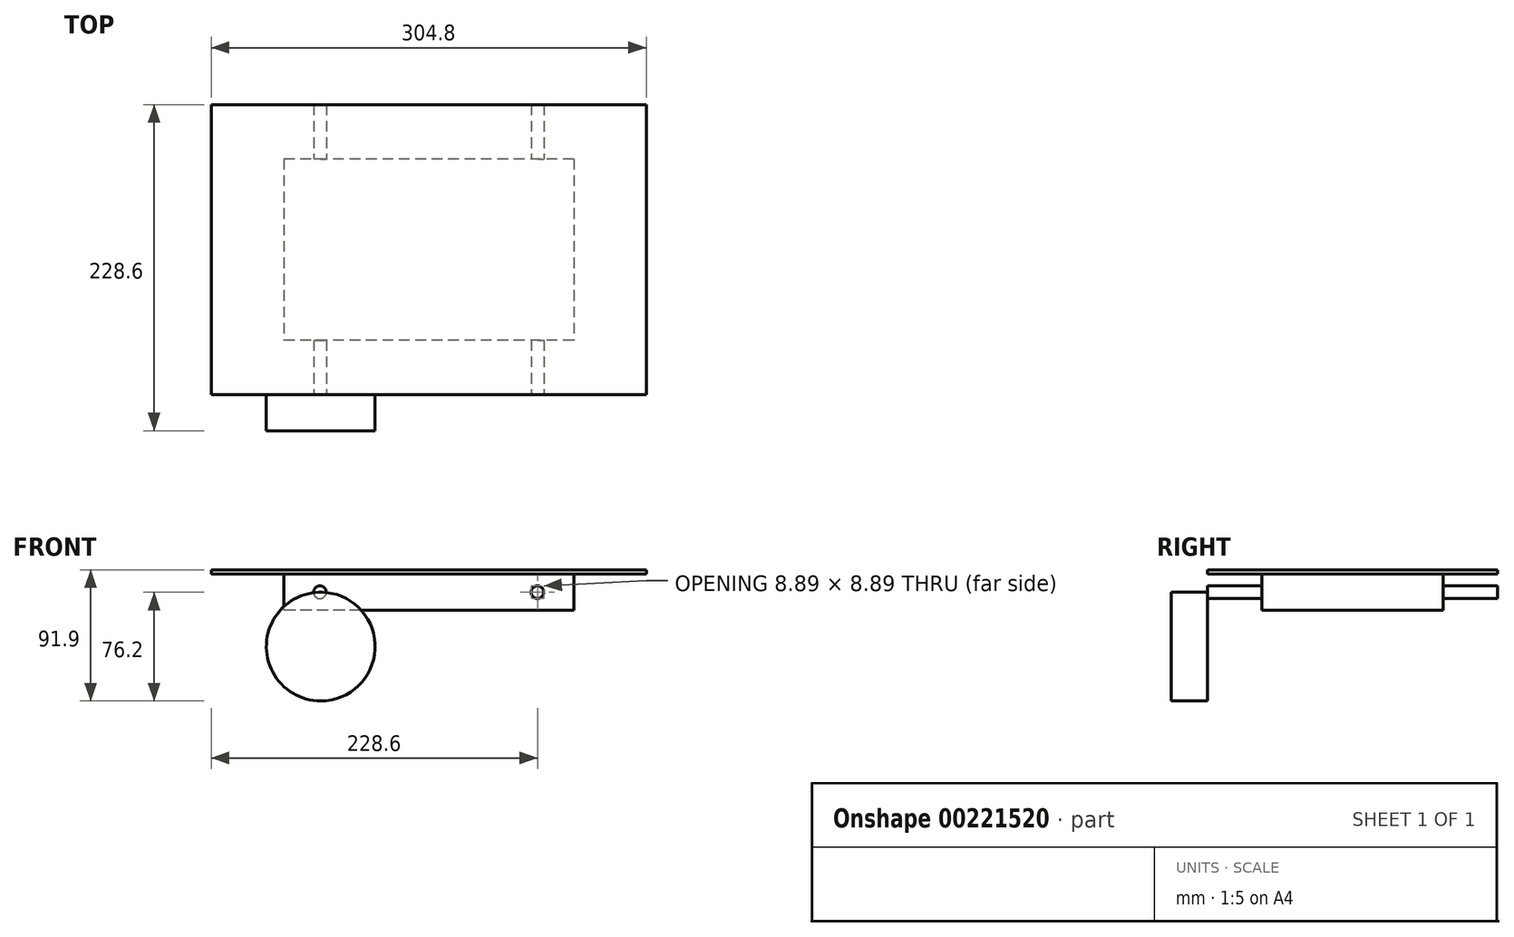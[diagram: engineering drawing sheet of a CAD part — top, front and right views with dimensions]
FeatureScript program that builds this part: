
annotation { "Feature Type Name" : "Feature", "Feature Type Description" : "" }
export const myFeature = defineFeature(function(context is Context, id is Id, definition is map)
    precondition{}
    {
        {
            var Q0;
            Q0=qCreatedBy(makeId("Top.planeOp"),FACE);
            var sketch = newSketch(context, id + "F0", { "sketchPlane" : qUnion([Q0])});
            skLineSegment(sketch, "E0.bottom", {"start": v(152.4, -101.6) * mm, "end": v(-152.4, -101.6) * mm});
            skLineSegment(sketch, "E0.top", {"start": v(152.4, 101.6) * mm, "end": v(-152.4, 101.6) * mm});
            skLineSegment(sketch, "E0.left", {"start": v(152.4, -101.6) * mm, "end": v(152.4, 101.6) * mm});
            skLineSegment(sketch, "E0.right", {"start": v(-152.4, -101.6) * mm, "end": v(-152.4, 101.6) * mm});
            skPoint(sketch, "E0.middle", {"position": v(0, 0) * mm});
            skSolve(sketch);
        }
        {
            var Q0;
            Q0 = qSketchRegion(id + "F0", true);
            extrude(context, id + "F1", {"entities" : qUnion([Q0]), "depth" : 3 * mm});
        }
        {
            var Q0;
            Q0=makeQuery(id+"F1.opExtrude","CAP_FACE",FACE,{"disambiguationData":[OSD([sQuery(id+"F0.wireOp",EDGE,"E0.bottom"),sQuery(id+"F0.wireOp",EDGE,"E0.top"),sQuery(id+"F0.wireOp",EDGE,"E0.left"),sQuery(id+"F0.wireOp",EDGE,"E0.right")])],"isStart":true});
            var sketch = newSketch(context, id + "F2", { "sketchPlane" : qUnion([Q0])});
            skLineSegment(sketch, "E1.bottom", {"start": v(101.6, -63.5) * mm, "end": v(-101.6, -63.5) * mm});
            skLineSegment(sketch, "E1.top", {"start": v(101.6, 63.5) * mm, "end": v(-101.6, 63.5) * mm});
            skLineSegment(sketch, "E1.left", {"start": v(101.6, -63.5) * mm, "end": v(101.6, 63.5) * mm});
            skLineSegment(sketch, "E1.right", {"start": v(-101.6, -63.5) * mm, "end": v(-101.6, 63.5) * mm});
            skPoint(sketch, "E1.middle", {"position": v(0, 0) * mm});
            skSolve(sketch);
        }
        {
            var Q0;
            Q0 = qSketchRegion(id + "F2", true);
            extrude(context, id + "F3", {"entities" : qUnion([Q0]), "operationType" : NewBodyOperationType.ADD, "depth" : 25.4 * mm});
        }
        {
            var Q0;
            Q0=qCreatedBy(makeId("Front.planeOp"),FACE);
            var sketch = newSketch(context, id + "F4", { "sketchPlane" : qUnion([Q0])});
            skCircle(sketch, "E2", {"center": v(-76.2, -12.7) * mm, "radius": 4.45 * mm});
            skCircle(sketch, "E3", {"center": v(76.2, -12.7) * mm, "radius": 4.45 * mm});
            skSolve(sketch);
        }
        {
            var Q0;
            Q0 = qSketchRegion(id + "F4", true);
            extrude(context, id + "F5", {"entities" : qUnion([Q0]), "operationType" : NewBodyOperationType.ADD, "endBound" : BoundingType.SYMMETRIC, "oppositeDirection" : true, "depth" : 203.2 * mm});
        }
        {
            var Q0;
            Q0=makeQuery(id+"F5.opExtrude","CAP_FACE",FACE,{"disambiguationData":[OSD([sQuery(id+"F4.wireOp",EDGE,"E2")])],"isStart":true});
            var sketch = newSketch(context, id + "F6", { "sketchPlane" : qUnion([Q0])});
            skCircle(sketch, "E4", {"center": v(-75.6, -50.8) * mm, "radius": 38.1 * mm});
            skPoint(sketch, "E4.first.point", {"position": v(-76.2, -12.7) * mm});
            skPoint(sketch, "E4.second.point", {"position": v(-74.95, -88.89) * mm});
            skPoint(sketch, "E4.third.point", {"position": v(-38.7, -60.28) * mm});
            skSolve(sketch);
        }
        {
            var Q0;
            Q0 = qSketchRegion(id + "F6", true);
            extrude(context, id + "F7", {"entities" : qUnion([Q0]), "operationType" : NewBodyOperationType.ADD, "depth" : 25.4 * mm});
        }
    });
